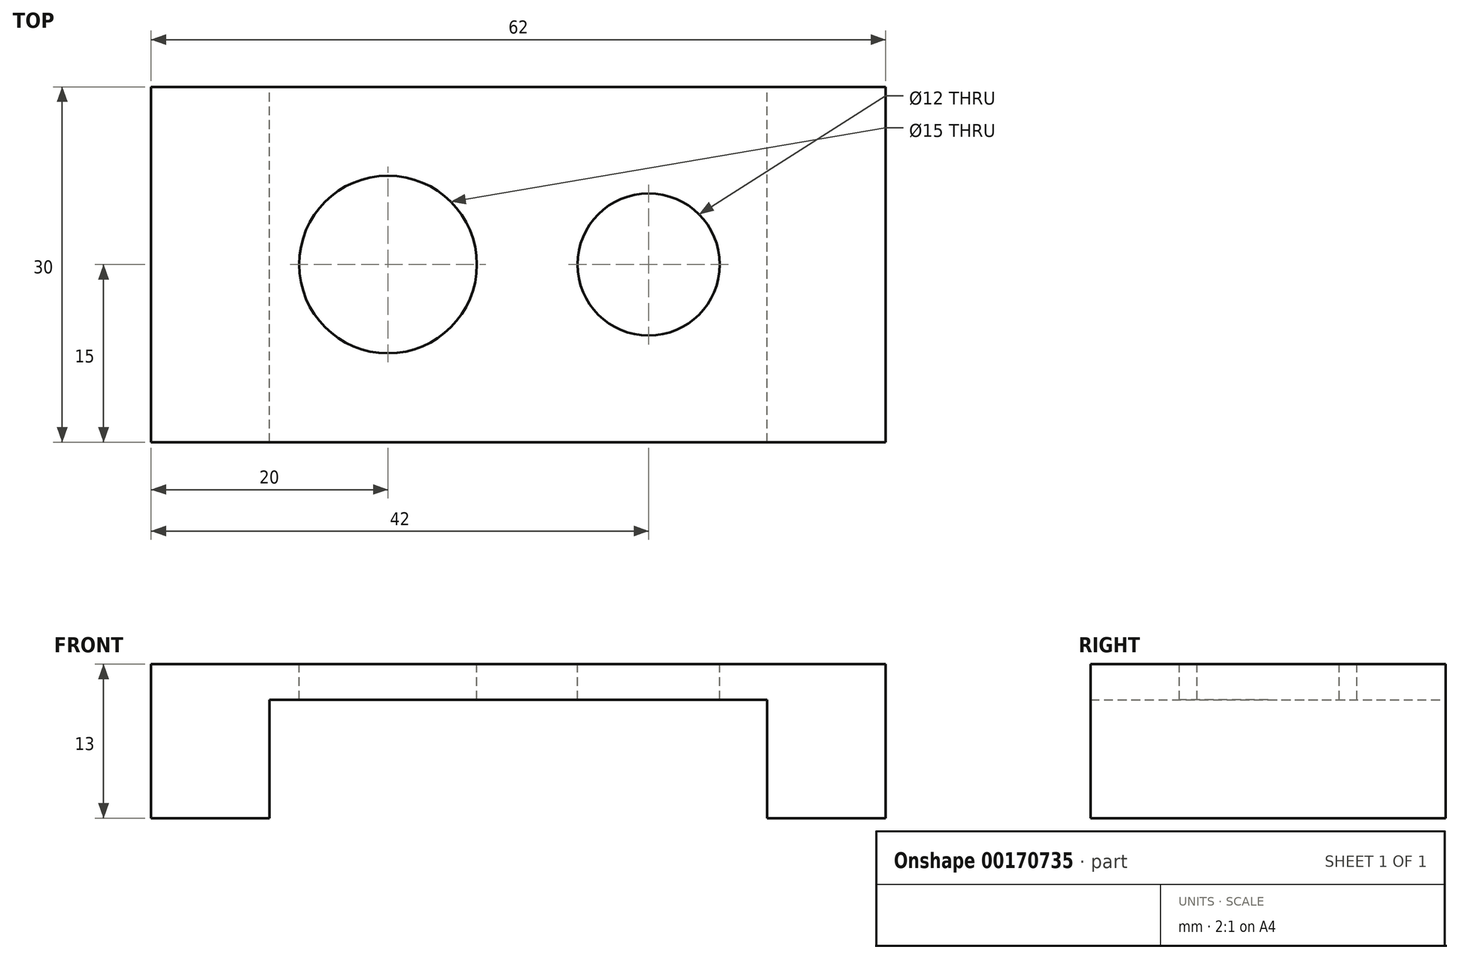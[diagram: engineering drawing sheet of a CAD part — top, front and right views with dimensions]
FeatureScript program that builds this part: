
annotation { "Feature Type Name" : "Feature", "Feature Type Description" : "" }
export const myFeature = defineFeature(function(context is Context, id is Id, definition is map)
    precondition{}
    {
        {
            var Q0;
            Q0=qCreatedBy(makeId("Front.planeOp"),FACE);
            var sketch = newSketch(context, id + "F0", { "sketchPlane" : qUnion([Q0])});
            skLineSegment(sketch, "E0", {"start": v(0, 0) * mm, "end": v(62, 0) * mm});
            skLineSegment(sketch, "E1", {"start": v(62, 0) * mm, "end": v(62, -13) * mm});
            skLineSegment(sketch, "E2", {"start": v(62, -13) * mm, "end": v(52, -13) * mm});
            skLineSegment(sketch, "E3", {"start": v(52, -13) * mm, "end": v(52, -3) * mm});
            skLineSegment(sketch, "E4", {"start": v(52, -3) * mm, "end": v(10, -3) * mm});
            skLineSegment(sketch, "E5", {"start": v(10, -3) * mm, "end": v(10, -13) * mm});
            skLineSegment(sketch, "E6", {"start": v(10, -13) * mm, "end": v(0, -13) * mm});
            skLineSegment(sketch, "E7", {"start": v(0, -13) * mm, "end": v(0, 0) * mm});
            skSolve(sketch);
        }
        {
            var Q0;
            Q0 = qSketchRegion(id + "F0", true);
            extrude(context, id + "F1", {"entities" : qUnion([Q0]), "depth" : 30 * mm});
        }
        {
            var Q0;
            Q0=makeQuery(id+"F1.opExtrude","SWEPT_FACE",FACE,{"disambiguationData":[OSD([sQuery(id+"F0.wireOp",EDGE,"E0")])]});
            var sketch = newSketch(context, id + "F2", { "sketchPlane" : qUnion([Q0])});
            skCircle(sketch, "E8", {"center": v(20, -15) * mm, "radius": 7.5 * mm});
            skPoint(sketch, "E8.centerSnap0", {"position": v(0, -15) * mm});
            skCircle(sketch, "E9", {"center": v(42, -15) * mm, "radius": 6 * mm});
            skPoint(sketch, "E9.centerSnap0", {"position": v(62, -15) * mm});
            skSolve(sketch);
        }
        {
            var Q0;
            Q0 = qSketchRegion(id + "F2", true);
            extrude(context, id + "F3", {"entities" : qUnion([Q0]), "operationType" : NewBodyOperationType.REMOVE, "endBound" : BoundingType.THROUGH_ALL, "oppositeDirection" : true, "depth" : 25 * mm});
        }
    });
